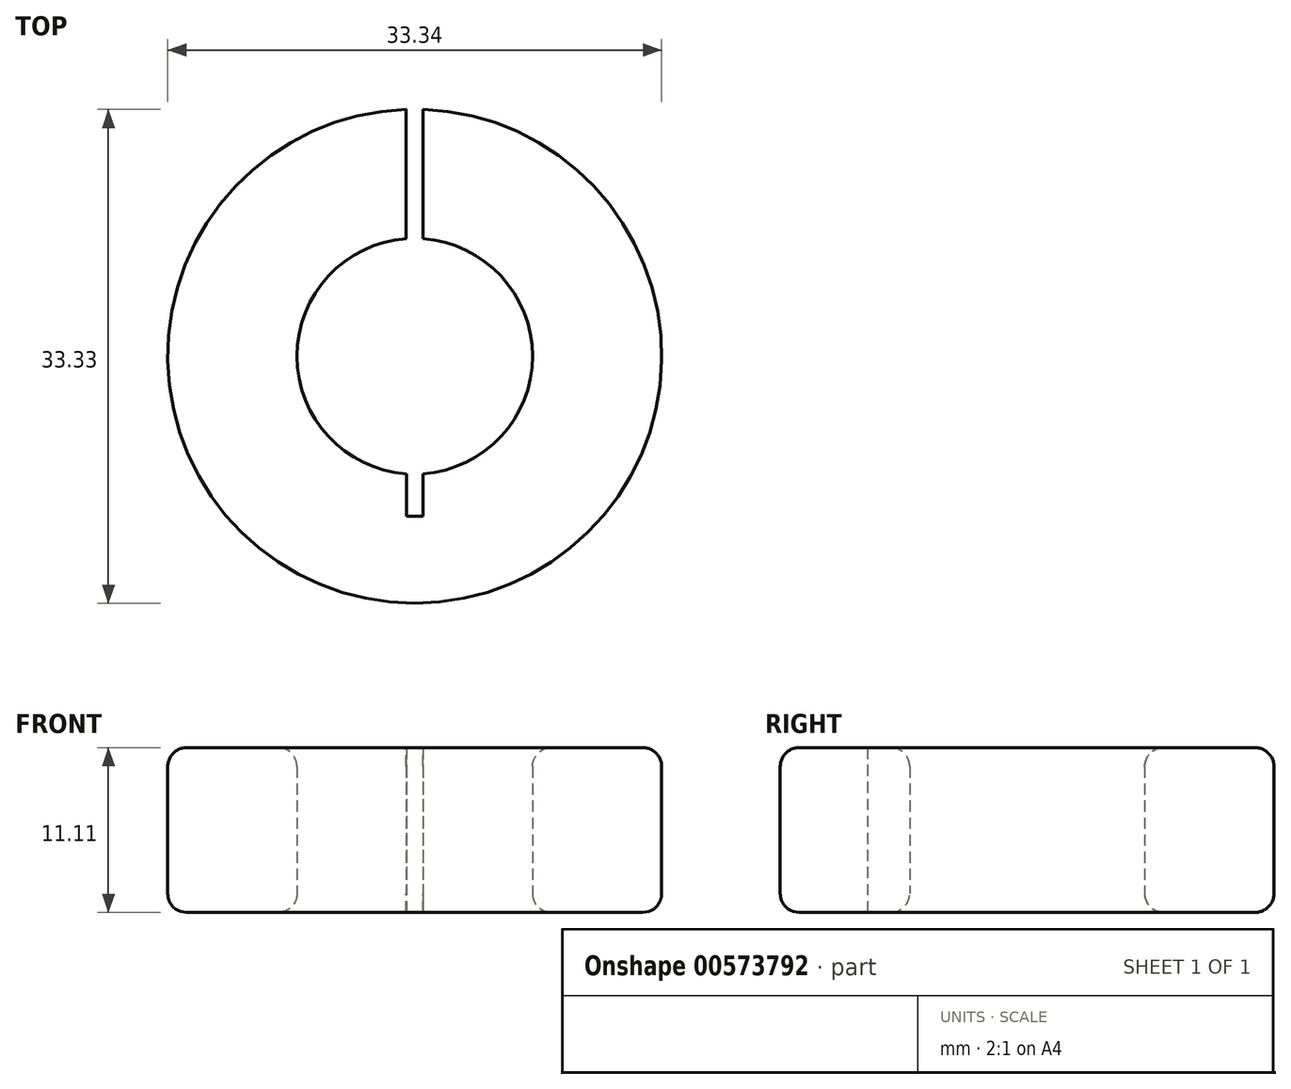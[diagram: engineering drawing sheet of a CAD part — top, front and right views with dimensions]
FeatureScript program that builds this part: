
annotation { "Feature Type Name" : "Feature", "Feature Type Description" : "" }
export const myFeature = defineFeature(function(context is Context, id is Id, definition is map)
    precondition{}
    {
        {
            var Q0;
            Q0=qCreatedBy(makeId("Top.planeOp"),FACE);
            var sketch = newSketch(context, id + "F0", { "sketchPlane" : qUnion([Q0])});
            skLineSegment(sketch, "E0.0", {"start": v(0.57, -10.8) * mm, "end": v(-0.57, -10.8) * mm});
            skArc(sketch, "E1.0.2", {"start": v(0.57, 7.93) * mm, "mid": v(7.95, 0) * mm, "end": v(0.57, -7.93) * mm});
            skArc(sketch, "E2", {"start": v(-0.57, 16.66) * mm, "mid": v(0, -16.67) * mm, "end": v(0.57, 16.66) * mm});
            skArc(sketch, "E3", {"start": v(-0.57, 7.93) * mm, "mid": v(-7.95, 0) * mm, "end": v(-0.57, -7.93) * mm});
            skLineSegment(sketch, "E4", {"start": v(-0.57, -7.93) * mm, "end": v(-0.57, -10.8) * mm});
            skLineSegment(sketch, "E5", {"start": v(0.57, -10.8) * mm, "end": v(0.57, -7.93) * mm});
            skLineSegment(sketch, "E6", {"start": v(-0.57, 16.66) * mm, "end": v(-0.57, 7.93) * mm});
            skLineSegment(sketch, "E7", {"start": v(0.57, 16.66) * mm, "end": v(0.57, 7.93) * mm});
            skCircle(sketch, "E8", {"center": v(0, 0) * mm, "radius": 7.95 * mm, "construction": true});
            skPoint(sketch, "E9", {"position": v(0, -10.8) * mm});
            skSolve(sketch);
        }
        {
            var Q0;
            Q0 = qSketchRegion(id + "F0", true);
            extrude(context, id + "F1", {"entities" : qUnion([Q0]), "depth" : 11.1 * mm, "offsetDistance" : 25.4 * mm});
        }
        {
            var Q0;
            Q0=makeQuery(id+"F1.opExtrude","CAP_EDGE",EDGE,{"disambiguationData":[OSD([sQuery(id+"F0.wireOp",EDGE,"E3")])],"isStart":false});
            var Q1;
            Q1=makeQuery(id+"F1.opExtrude","CAP_EDGE",EDGE,{"disambiguationData":[OSD([sQuery(id+"F0.wireOp",EDGE,"E3")])],"isStart":true});
            var Q2;
            Q2=makeQuery(id+"F1.opExtrude","CAP_EDGE",EDGE,{"disambiguationData":[OSD([sQuery(id+"F0.wireOp",EDGE,"E2")])],"isStart":false});
            var Q3;
            Q3=makeQuery(id+"F1.opExtrude","CAP_EDGE",EDGE,{"disambiguationData":[OSD([sQuery(id+"F0.wireOp",EDGE,"E2")])],"isStart":true});
            var Q4;
            Q4=makeQuery(id+"F1.opExtrude","CAP_EDGE",EDGE,{"disambiguationData":[OSD([sQuery(id+"F0.wireOp",EDGE,"63bfebc4-1374-4913-96d9-5cd23f8d37b3.trimOffspring")])],"isStart":true});
            var Q5;
            Q5=makeQuery(id+"F1.opExtrude","CAP_EDGE",EDGE,{"disambiguationData":[OSD([sQuery(id+"F0.wireOp",EDGE,"63bfebc4-1374-4913-96d9-5cd23f8d37b3.trimOffspring")])],"isStart":false});
            var Q6;
            Q6=makeQuery(id+"F1.opExtrude","CAP_EDGE",EDGE,{"disambiguationData":[OSD([sQuery(id+"F0.wireOp",EDGE,"E1.0.2")])],"isStart":false});
            var Q7;
            Q7=makeQuery(id+"F1.opExtrude","CAP_EDGE",EDGE,{"disambiguationData":[OSD([sQuery(id+"F0.wireOp",EDGE,"E1.0.2")])],"isStart":true});
            fillet(context, id + "F2", {"entities" : qUnion([Q0, Q1, Q2, Q3, Q4, Q5, Q6, Q7]), "radius" : 1.27 * mm, "tangentPropagation" : true, "allowEdgeOverflow" : false});
        }
    });
